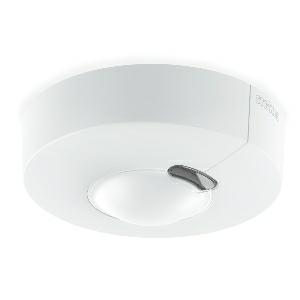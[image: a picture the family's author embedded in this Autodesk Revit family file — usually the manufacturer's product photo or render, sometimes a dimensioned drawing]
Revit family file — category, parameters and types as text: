
# Revit family: hf_3360_033699
name_source: partatom
category: Elektroinstallationen
revit_build: Autodesk Revit 2016 (Build: 20190508_0715(x64)
units: mm (PartAtom-declared; Revit-internal decimal feet)

## family parameters
Basisbauteil = Fläche
Beim Laden mit Abzugskörper schneiden = Nein
Bemaßung runder Anschluss = Durchmesser verwenden
Beschriftungsausrichtung beibehalten = Nein
Gemeinsam genutzt = Nein
Raumberechnungspunkt = Nein
Teiletyp = Normal

## types (1)
- HF 3360
    Apparent Load = 0 VA
    Beschreibung = Type: Motion detectors; Dimensions (Ø x H): 126 x 52 mm; Mains power supply: 220 – 240 V / 50 – 60 Hz; Sensor Technology: High frequency; Application, place: Indoors; Application, room: function room / ancillary room, stairwell, WC / washroom, multi-storey / underground car park, Indoors; Installation site: wall, ceiling, corner; Installation: Surface wiring; HF-system: 5,8 GHz; Electronic scalability: Yes; Mechanical scalability: No; Mounting height: 2,00 – 4,00 m; Optimum mounting height: 2,8 m; Detection: also through glass, wood and stud walls; Detection angle: 360 °; Angle of aperture: 140 °; Sneak-by guard: Yes; Reach, radial: Ø 8 m (50 m²); Reach, tangential: Ø 8 m (50 m²); Twilight setting TEACH: Yes; Twilight setting: 2 – 1000 lx; Time setting: 5 sec – 15 min; Constant-lighting control: No; Basic light level function: No; Functions: Normal / test mode, Manual ON / ON-OFF; Settings via: Remote control, Potentiometers, Smart Remote; With remote control: No; Interconnection: Yes; IP-rating: IP54; Material: Plastic; Ambient temperature: -20 – 50 °C; Colour: white; Colour, RAL: 9003; Manufacturer's Warranty: 5 years; Version: PF - surface, rd.; PU1, EAN: 4007841033699
    Height = 0 mm  [stored 0 ft]
    Hersteller = Steinel
    Length = 126 mm
    ModVariant = Nein
    Modell = 033699
    Mounting Type = Surface mounted
    Number of Poles = 1
    OnlyDefault = Ja
    Power Factor = 1
    Product Name = HF 3360
    Product group = Sensor-switched indoor light
    ProductGroupID = 30
    Protection Class = Protection class
    Protection Degree = IP 54
    RlxData = <blob elided: 37225 chars, md5=7eab1c43>
    SensorDataFile = {"IESDataFiles":[]}
    Typenbild = produkt1_033699.jpg
    Typenkommentare = Product without accessories
    URL = http://relux.com
    VarID = ---
    Voltage = 0 V
    Vorgabe-Ansicht = 1800 mm
    Weight = 0.00 kg
    Width = 0 mm  [stored 0 ft]

note: [stored X ft] marks values corroborated as IEEE doubles in the binary element streams (Revit-internal decimal feet)

## geometry (parser evidence)
native form markers: Sweep x9
no freeform markers — native parametric forms only
